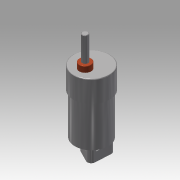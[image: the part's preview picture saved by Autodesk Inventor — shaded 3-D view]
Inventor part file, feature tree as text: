
AUTODESK INVENTOR PART (.ipt)
format: ipt  version: 2016 (Build 200138000, 138)  size: 226,816 bytes
history: native  units: in
note: dims shown in document units (in); Inventor stores cm internally (conversion verified against a paired STEP export)
features: other x4, sketch x4
ambient origin geometry x8: Origin, YZ Plane, XZ Plane, XY Plane, X Axis, Y Axis, Z Axis, Center Point
bodies: Solid1 (feature_tree), Solid2 (feature_tree)
feature tree (8):
  other  "Tetrix motor.ipt"
  other  "DC_MOTOR_2011::Tetrix motor.ipt"
  other  "Solid2::Tetrix motor.ipt"
  other  "TaggingFeature1"
  sketch  "Sketch1"  dims[d0=0.3937in]
  sketch  "Sketch2"  dims[d1=0.5909in d3=0.3436in d5=0.4528in d6=0.4528in d7=0.1654in d8=0.0in d9=0.748in d11=0.4331in d12=0.3661in d13=0.0in d14=0.2165in d16=0.0472in d17=0.0in d18=0.0197in d19=0.0787in d20=0.1181in d21=0.1181in d22=0.5906in d23=0.0in]
  sketch  "Sketch3"
  sketch  "Sketch4"
